# Revit family: IZF 6420
name_source: partatom
category: Specialty Equipment
revit_build: Autodesk Revit 2017 (Build: 20160225_1515(x64)
units: mm (PartAtom-declared; Revit-internal decimal feet)

## family parameters
Cut with Voids When Loaded = Yes
Host = Face
Part Type = Normal
Room Calculation Point = No
Round Connector Dimension = Use Diameter
Shared = No

## types (1)
- IZF 6420
    Alto encastre = 80 mm  [stored 0.262467 ft]
    Ancho encastre = 560 mm  [stored 1.83727 ft]
    Ca_1_Cable Conexión Tri-fásica = Yes
    Ca_1_Frecuencia Hz. = 50
    Ca_1_Potencia W. = 7400
    Ca_1_Tensión 220/240 V. = 220
    Ca_2_Inducción Oval = 235 x 180 mm
    Ca_2_Inducción ø 145 = 1
    Ca_2_Inducción ø 210 = 1
    Ca_3_Bloqueo de panel = Yes
    Ca_3_Detector de recipientes = Yes
    Ca_3_Función Power Plus = Yes
    Ca_3_Función Stop & Go = Yes
    Ca_3_Indicador de calor residual = Yes
    Ca_3_Keep Warm = Yes
    Ca_3_Optimizador de recipientes = Yes
    Ca_3_Programador independiente cada plato = Yes
    Ca_3_Quick Boiling = 1
    Ca_3_Synchro = 2
    Ca_3_Terminación = Biselada Frontal
    Ca_3_Touch Control (Slider) = Yes
    Ca_Alto = 0 mm  [stored 0 ft]
    Ca_Alto Interior = 0 mm  [stored 0 ft]
    Ca_Ancho = 600 mm
    Ca_Ancho Interior = 560 mm  [stored 1.83727 ft]
    Ca_Creado por = Catálogo Arquitectura
    Ca_Código Catálogo Arquitectura = 465_TEK_020
    Ca_Código EAN = 8421152148785
    Ca_Código del Producto = 10210180
    Ca_Especificaciones Técnicas = Encimera por inducción empotrable para cocina modelo IZF 6420
    Ca_Fabricante = Teka
    Ca_Instalación = Empotrable
    Ca_Itemizado CDT = E 08 06 02
    Ca_Masterformat = 11 30 13.13
    Ca_Material Principal = Cristal vitrocerámico biselado frontal
    Ca_Medidas de embalaje = 103 x 659 x 553 mm
    Ca_País de Fabricación = Turquía
    Ca_Peso = 11,8 kg
    Ca_Producto = Encimera inducción IZF 6420
    Ca_Profundidad = 510 mm  [stored 1.67323 ft]
    Ca_Profundidad Interior = 490 mm
    Ca_Representante = Teka
    Ca_Teléfono = 99821 1017
    Ca_Usos = Encimera por inducción empotrable para mueble de cocina
    Ca_Web del Fabricante = www.teka.cl
    Ca_Web del Representante = www.teka.cl
    Cubierta encimera = Teka_Vidrio Encimera Satinado
    Default Elevation = 1219.2 mm  [stored 4 ft]
    Description = Encimera por inducción empotrable para mueble de cocina
    Interior encimera = Teka_Aluminio
    Manufacturer = Teka
    Model = IZF 6420
    Profundiadad encimera = 40 mm  [stored 0.131234 ft]
    Profundidad encastre = 470 mm
    URL = www.teka.cl

note: [stored X ft] marks values corroborated as IEEE doubles in the binary element streams (Revit-internal decimal feet)
